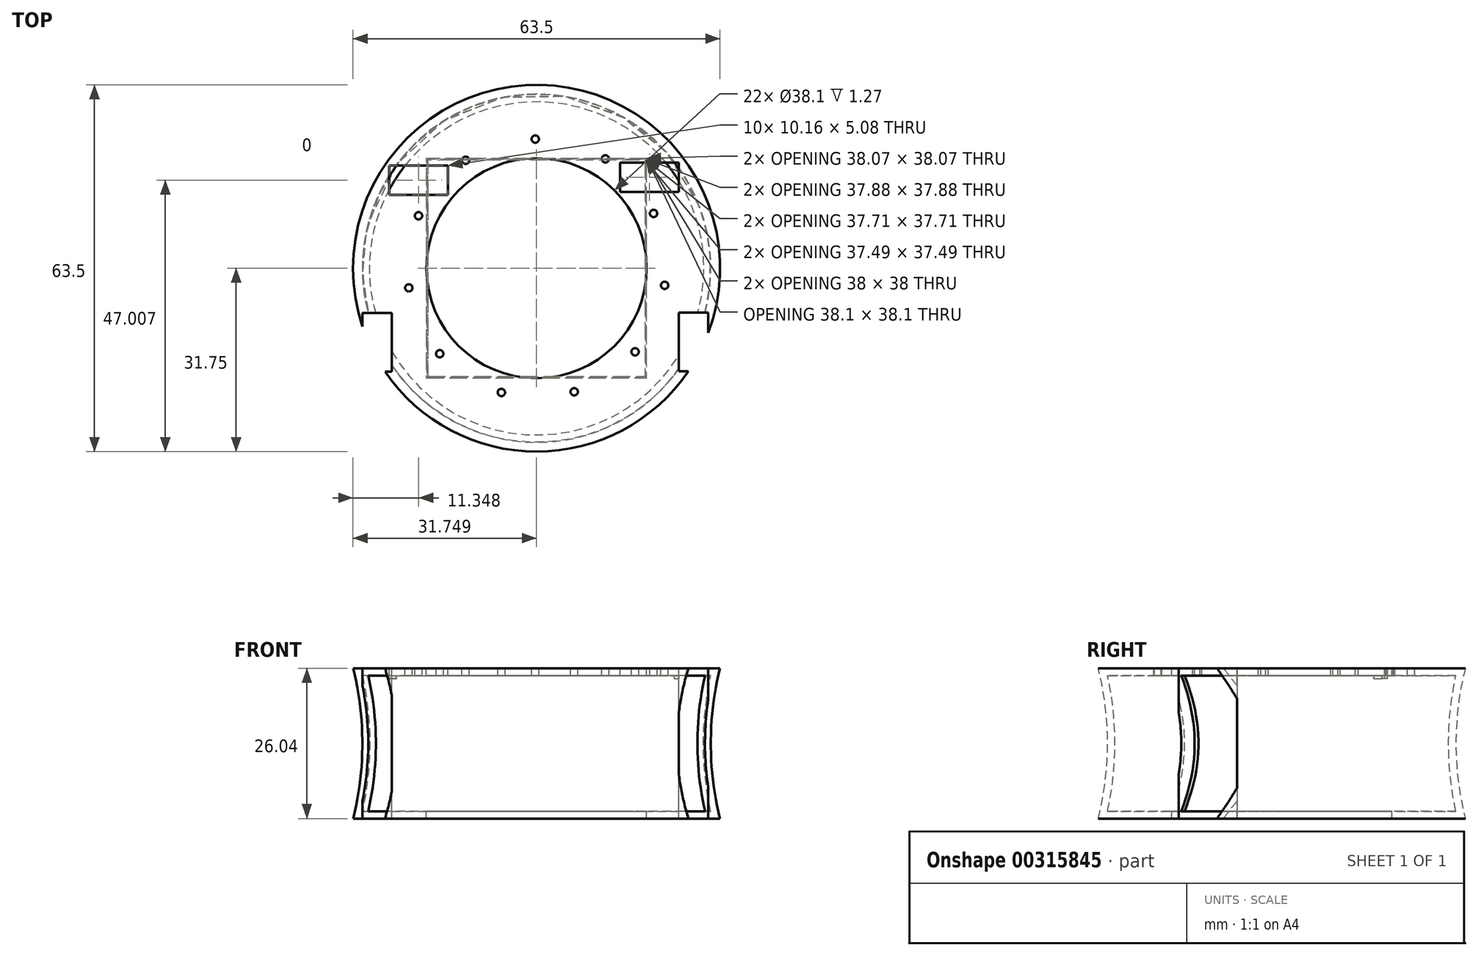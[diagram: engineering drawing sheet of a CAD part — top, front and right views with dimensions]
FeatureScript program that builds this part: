
annotation { "Feature Type Name" : "Feature", "Feature Type Description" : "" }
export const myFeature = defineFeature(function(context is Context, id is Id, definition is map)
    precondition{}
    {
        {
            var Q0;
            Q0=qCreatedBy(makeId("Front.planeOp"),FACE);
            var sketch = newSketch(context, id + "F0", { "sketchPlane" : qUnion([Q0])});
            skArc(sketch, "E0", {"start": v(-60.24, 12.57) * mm, "mid": v(-58.63, 25.6) * mm, "end": v(-60.24, 38.6) * mm});
            skLineSegment(sketch, "E1", {"start": v(-47.54, 38.6) * mm, "end": v(-47.54, 12.57) * mm});
            skLineSegment(sketch, "E2", {"start": v(-28.5, 38.32) * mm, "end": v(-28.5, 12.29) * mm});
            skArc(sketch, "E3", {"start": v(-47.54, 38.6) * mm, "mid": v(-53.89, 40.35) * mm, "end": v(-60.24, 38.6) * mm});
            skLineSegment(sketch, "E4", {"start": v(-60.24, 38.6) * mm, "end": v(-47.54, 38.6) * mm});
            skLineSegment(sketch, "E5", {"start": v(-60.24, 12.57) * mm, "end": v(-47.54, 12.57) * mm});
            skSolve(sketch);
        }
        {
            var Q0;
            Q0=makeQuery(id+"F0.imprint","IMPRINT",FACE,{"disambiguationData":[TD([[makeQuery(id+"F0.imprint","IMPRINT",EDGE,{"derivedFrom":sQuery(id+"F0.wireOp",EDGE,"E0")}),-1.0]])]});
            var Q1;
            Q1=sQuery(id+"F0.wireOp",EDGE,"E2");
            revolve(context, id + "F1", {"entities" : qUnion([Q0]), "axis" : qUnion([Q1]), "revolveType" : RevolveType.FULL});
        }
        {
            var Q0;
            Q0=makeQuery(id+"F1.opRevolve","SWEPT_FACE",FACE,{"disambiguationData":[OSD([sQuery(id+"F0.wireOp",EDGE,"E1")])]});
            shell(context, id + "F2", {"entities" : qUnion([Q0]), "thickness" : 1.27 * mm});
        }
        {
            var Q0;
            Q0=makeQuery(id+"F1.opRevolve","SWEPT_FACE",FACE,{"disambiguationData":[OSD([sQuery(id+"F0.wireOp",EDGE,"E4")])]});
            var sketch = newSketch(context, id + "F3", { "sketchPlane" : qUnion([Q0])});
            skCircle(sketch, "E6", {"center": v(-28.71, 22.36) * mm, "radius": 0.64 * mm});
            skSolve(sketch);
        }
        {
            var Q0;
            Q0=sQuery(id+"F3.wireOp",VERTEX,"E6.center");
            var Q1;
            Q1=makeQuery(id+"F1.opRevolve","SWEPT_BODY",BODY,{"disambiguationData":[OSD([sQuery(id+"F0.wireOp",EDGE,"E0"),sQuery(id+"F0.wireOp",EDGE,"MX34I96n-xlW5-kaZN-7TZv-NTZrBtyPyz58"),sQuery(id+"F0.wireOp",EDGE,"E1"),sQuery(id+"F0.wireOp",EDGE,"N5HLZdBb-6Rrh-yp8l-RINS-z0ERBs1BBXMQ")])]});
            hole(context, id + "F4", {"style" : HoleStyle.SIMPLE, "endStyle" : HoleEndStyle.BLIND, "holeDiameter" : 1.27 * mm, "holeDepth" : 5.08 * mm, "tappedDepth" : 12.7 * mm, "tapClearance" : 3, "startFromSketch" : true, "locations" : qUnion([Q0]), "scope" : qUnion([Q1])});
        }
        {
            var Q0;
            Q0=makeQuery(id+"F1.opRevolve","SWEPT_BODY",BODY,{"disambiguationData":[OSD([sQuery(id+"F0.wireOp",EDGE,"E0"),sQuery(id+"F0.wireOp",EDGE,"MX34I96n-xlW5-kaZN-7TZv-NTZrBtyPyz58"),sQuery(id+"F0.wireOp",EDGE,"E1"),sQuery(id+"F0.wireOp",EDGE,"N5HLZdBb-6Rrh-yp8l-RINS-z0ERBs1BBXMQ")])]});
            var Q1;
            Q1=makeQuery(id+"F1.opRevolve","SWEPT_BODY",BODY,{"disambiguationData":[OSD([sQuery(id+"F0.wireOp",EDGE,"E0"),sQuery(id+"F0.wireOp",EDGE,"MX34I96n-xlW5-kaZN-7TZv-NTZrBtyPyz58"),sQuery(id+"F0.wireOp",EDGE,"E1"),sQuery(id+"F0.wireOp",EDGE,"E4")])]});
            var Q2;
            Q2=makeQuery(id+"F1.opRevolve","SWEPT_EDGE",EDGE,{"disambiguationData":[OSD([sQuery(id+"F0.wireOp",EDGE,"E1"),sQuery(id+"F0.wireOp",EDGE,"E3"),sQuery(id+"F0.wireOp",EDGE,"N5HLZdBb-6Rrh-yp8l-RINS-z0ERBs1BBXMQ")])]});
            circularPattern(context, id + "F5", {"entities" : qUnion([Q0, Q1]), "axis" : qUnion([Q2]), "angle" : 360 * degree, "instanceCount" : 11, "equalSpace" : true});
        }
        {
            var Q0;
            Q0=makeQuery(id+"F1.opRevolve","SWEPT_FACE",FACE,{"disambiguationData":[OSD([sQuery(id+"F0.wireOp",EDGE,"E4")])]});
            var sketch = newSketch(context, id + "F6", { "sketchPlane" : qUnion([Q0])});
            skLineSegment(sketch, "E7.bottom", {"start": v(-14.04, 18.3) * mm, "end": v(-3.88, 18.3) * mm});
            skLineSegment(sketch, "E7.top", {"start": v(-14.04, 13.21) * mm, "end": v(-3.88, 13.21) * mm});
            skLineSegment(sketch, "E7.left", {"start": v(-14.04, 18.3) * mm, "end": v(-14.04, 13.21) * mm});
            skLineSegment(sketch, "E7.right", {"start": v(-3.88, 18.3) * mm, "end": v(-3.88, 13.21) * mm});
            skSolve(sketch);
        }
        {
            var Q0;
            Q0=makeQuery(id+"F6.imprint","IMPRINT",FACE,{"disambiguationData":[TD([[makeQuery(id+"F6.imprint","IMPRINT",EDGE,{"derivedFrom":sQuery(id+"F6.wireOp",EDGE,"E7.bottom")}),-1.0]])]});
            extrude(context, id + "F7", {"entities" : qUnion([Q0]), "operationType" : NewBodyOperationType.REMOVE, "oppositeDirection" : true, "depth" : 1.78 * mm});
        }
        {
            var Q0;
            Q0=makeQuery(id+"F1.opRevolve","SWEPT_FACE",FACE,{"disambiguationData":[OSD([sQuery(id+"F0.wireOp",EDGE,"E4")])]});
            var sketch = newSketch(context, id + "F8", { "sketchPlane" : qUnion([Q0])});
            skLineSegment(sketch, "E8.bottom", {"start": v(-43.81, 12.72) * mm, "end": v(-53.97, 12.72) * mm});
            skLineSegment(sketch, "E8.top", {"start": v(-43.81, 17.8) * mm, "end": v(-53.97, 17.8) * mm});
            skLineSegment(sketch, "E8.left", {"start": v(-43.81, 12.72) * mm, "end": v(-43.81, 17.8) * mm});
            skLineSegment(sketch, "E8.right", {"start": v(-53.97, 12.72) * mm, "end": v(-53.97, 17.8) * mm});
            skSolve(sketch);
        }
        {
            var Q0;
            Q0=makeQuery(id+"F8.imprint","IMPRINT",FACE,{"disambiguationData":[TD([[makeQuery(id+"F8.imprint","IMPRINT",EDGE,{"derivedFrom":sQuery(id+"F8.wireOp",EDGE,"E8.bottom")}),-1.0]])]});
            extrude(context, id + "F9", {"entities" : qUnion([Q0]), "operationType" : NewBodyOperationType.REMOVE, "oppositeDirection" : true, "depth" : 1.78 * mm});
        }
        {
            var Q0;
            Q0=makeQuery(id+"F1.opRevolve","SWEPT_FACE",FACE,{"disambiguationData":[OSD([sQuery(id+"F0.wireOp",EDGE,"E4")])]});
            var sketch = newSketch(context, id + "F10", { "sketchPlane" : qUnion([Q0])});
            skLineSegment(sketch, "E9.bottom", {"start": v(-58.59, -7.74) * mm, "end": v(-53.5, -7.74) * mm});
            skLineSegment(sketch, "E9.top", {"start": v(-58.59, -17.9) * mm, "end": v(-53.5, -17.9) * mm});
            skLineSegment(sketch, "E9.left", {"start": v(-58.59, -7.74) * mm, "end": v(-58.59, -17.9) * mm});
            skLineSegment(sketch, "E9.right", {"start": v(-53.5, -7.74) * mm, "end": v(-53.5, -17.9) * mm});
            skLineSegment(sketch, "E10.bottom", {"start": v(-3.87, -7.68) * mm, "end": v(1.21, -7.68) * mm});
            skLineSegment(sketch, "E10.top", {"start": v(-3.87, -17.84) * mm, "end": v(1.21, -17.84) * mm});
            skLineSegment(sketch, "E10.left", {"start": v(-3.87, -7.68) * mm, "end": v(-3.87, -17.84) * mm});
            skLineSegment(sketch, "E10.right", {"start": v(1.21, -7.68) * mm, "end": v(1.21, -17.84) * mm});
            skSolve(sketch);
        }
        {
            var Q0;
            {var subQ1=sQuery(id+"F10.wireOp",EDGE,"E9.bottom");Q0=makeQuery(id+"F10.imprint","IMPRINT",FACE,{"disambiguationData":[TD([[makeQuery(id+"F10.imprint","IMPRINT",EDGE,{"derivedFrom":subQ1}),-1.0]])]});}
            var Q1;
            {var subQ0=sQuery(id+"F10.wireOp",EDGE,"E9.left");var subQ1=sQuery(id+"F10.wireOp",EDGE,"E9.top");var subQ2=makeQuery(id+"F10.imprint","INTERSECT",VERTEX,{"derivedFrom":[subQ1,subQ0]});Q1=makeQuery(id+"F10.imprint","IMPRINT",FACE,{"disambiguationData":[TD([[makeQuery(id+"F10.imprint","IMPRINT",EDGE,{"disambiguationData":[TD([[subQ2,-1.0]])],"derivedFrom":subQ1}),1.0]])]});}
            var Q2;
            {var subQ1=sQuery(id+"F10.wireOp",EDGE,"E10.bottom");Q2=makeQuery(id+"F10.imprint","IMPRINT",FACE,{"disambiguationData":[TD([[makeQuery(id+"F10.imprint","IMPRINT",EDGE,{"derivedFrom":subQ1}),-1.0]])]});}
            var Q3;
            {var subQ0=sQuery(id+"F10.wireOp",EDGE,"E10.right");var subQ1=sQuery(id+"F10.wireOp",EDGE,"E10.top");var subQ2=makeQuery(id+"F10.imprint","INTERSECT",VERTEX,{"derivedFrom":[subQ1,subQ0]});Q3=makeQuery(id+"F10.imprint","IMPRINT",FACE,{"disambiguationData":[TD([[makeQuery(id+"F10.imprint","IMPRINT",EDGE,{"disambiguationData":[TD([[subQ2,1.0]])],"derivedFrom":subQ1}),1.0]])]});}
            extrude(context, id + "F11", {"entities" : qUnion([Q0, Q1, Q2, Q3]), "operationType" : NewBodyOperationType.REMOVE, "oppositeDirection" : true, "depth" : 26.03 * mm});
        }
    });
